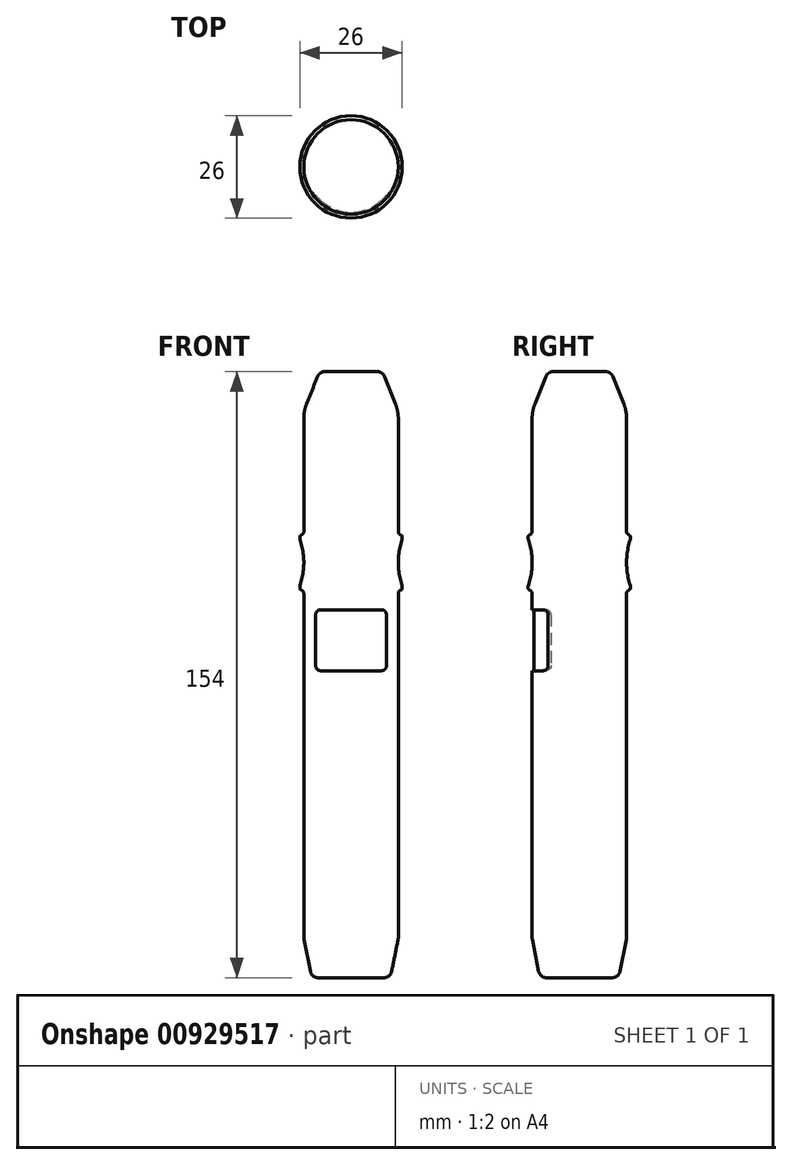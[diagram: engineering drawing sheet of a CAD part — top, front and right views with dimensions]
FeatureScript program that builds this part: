
annotation { "Feature Type Name" : "Feature", "Feature Type Description" : "" }
export const myFeature = defineFeature(function(context is Context, id is Id, definition is map)
    precondition{}
    {
        {
            var Q0;
            Q0=qCreatedBy(makeId("Top.planeOp"),FACE);
            var sketch = newSketch(context, id + "F0", { "sketchPlane" : qUnion([Q0])});
            skCircle(sketch, "E0", {"center": v(0, 0) * mm, "radius": 12 * mm});
            skSolve(sketch);
        }
        {
            var Q0;
            Q0 = qSketchRegion(id + "F0", true);
            extrude(context, id + "F1", {"entities" : qUnion([Q0]), "depth" : 154 * mm, "offsetDistance" : 25 * mm});
        }
        {
            var Q0;
            Q0=makeQuery(id+"F1.opExtrude","CAP_EDGE",EDGE,{"disambiguationData":[OSD([sQuery(id+"F0.wireOp",EDGE,"E0")])],"isStart":true});
            chamfer(context, id + "F2", {"entities" : qUnion([Q0]), "chamferType" : ChamferType.TWO_OFFSETS, "width1" : 10 * mm, "oppositeDirection" : false, "width2" : 2 * mm, "tangentPropagation" : true});
        }
        {
            var Q0;
            Q0=makeQuery(id+"F1.opExtrude","CAP_EDGE",EDGE,{"disambiguationData":[OSD([sQuery(id+"F0.wireOp",EDGE,"E0")])],"isStart":false});
            chamfer(context, id + "F3", {"entities" : qUnion([Q0]), "chamferType" : ChamferType.TWO_OFFSETS, "width1" : 4 * mm, "oppositeDirection" : false, "width2" : 10 * mm, "tangentPropagation" : true});
        }
        {
            var Q0;
            Q0=qCreatedBy(makeId("Front.planeOp"),FACE);
            var sketch = newSketch(context, id + "F4", { "sketchPlane" : qUnion([Q0])});
            skLineSegment(sketch, "E1", {"start": v(0, 112.5) * mm, "end": v(-12.5, 112.5) * mm});
            skLineSegment(sketch, "E2", {"start": v(-13, 112) * mm, "end": v(-13, 111.5) * mm});
            skLineSegment(sketch, "E3", {"start": v(-13, 99.5) * mm, "end": v(-13, 99) * mm});
            skLineSegment(sketch, "E4", {"start": v(-12.5, 98.5) * mm, "end": v(0, 98.5) * mm});
            skLineSegment(sketch, "E5", {"start": v(0, 98.5) * mm, "end": v(0, 112.5) * mm});
            skLineSegment(sketch, "E6", {"start": v(-12, 10) * mm, "end": v(-12, 110) * mm, "construction": true});
            skArc(sketch, "E7", {"start": v(-13, 99.5) * mm, "mid": v(-12, 105.5) * mm, "end": v(-13, 111.5) * mm});
            skPoint(sketch, "E8.visualSharp", {"position": v(-13, 112.5) * mm});
            skArc(sketch, "E8.filletArc", {"start": v(-12.5, 112.5) * mm, "mid": v(-12.85, 112.35) * mm, "end": v(-13, 112) * mm});
            skPoint(sketch, "E9.visualSharp", {"position": v(-13, 98.5) * mm});
            skArc(sketch, "E9.filletArc", {"start": v(-13, 99) * mm, "mid": v(-12.85, 98.65) * mm, "end": v(-12.5, 98.5) * mm});
            skSolve(sketch);
        }
        {
            var Q0;
            Q0 = qSketchRegion(id + "F4", true);
            var Q1;
            Q1=sQuery(id+"F4.wireOp",EDGE,"E5");
            revolve(context, id + "F5", {"operationType" : NewBodyOperationType.ADD, "surfaceOperationType" : NewSurfaceOperationType.NEW, "entities" : qUnion([Q0]), "axis" : qUnion([Q1]), "revolveType" : RevolveType.FULL});
        }
        {
            var Q0;
            Q0=makeQuery(id+"F5.opRevolve","SWEPT_EDGE",EDGE,{"disambiguationData":[OSD([sQuery(id+"F4.wireOp",EDGE,"E1"),sQuery(id+"F4.wireOp",EDGE,"E2")])]});
            var Q1;
            Q1=makeQuery(id+"F5.opRevolve","SWEPT_EDGE",EDGE,{"disambiguationData":[OSD([sQuery(id+"F4.wireOp",EDGE,"E2"),sQuery(id+"F4.wireOp",EDGE,"noVHmOIS-iAvs-KDMn-7KQd-Wlyn27HH3uOn")])]});
            var Q2;
            Q2=makeQuery(id+"F5.opRevolve","SWEPT_EDGE",EDGE,{"disambiguationData":[OSD([sQuery(id+"F4.wireOp",EDGE,"rKwzJUQm-pqnW-oJ42-K8gI-ygzuSZhMsq8l"),sQuery(id+"F4.wireOp",EDGE,"E3")])]});
            var Q3;
            Q3=makeQuery(id+"F5.opRevolve","SWEPT_EDGE",EDGE,{"disambiguationData":[OSD([sQuery(id+"F4.wireOp",EDGE,"E3"),sQuery(id+"F4.wireOp",EDGE,"E4")])]});
            var Q4;
            Q4=makeQuery(id+"F5.opRevolve","SWEPT_EDGE",EDGE,{"disambiguationData":[OSD([sQuery(id+"F4.wireOp",EDGE,"vrmqeYjg-Eb0b-bUPp-PHIE-IZj6HfNofiIo"),sQuery(id+"F4.wireOp",EDGE,"rKwzJUQm-pqnW-oJ42-K8gI-ygzuSZhMsq8l")])]});
            var Q5;
            Q5=makeQuery(id+"F5.opRevolve","SWEPT_EDGE",EDGE,{"disambiguationData":[OSD([sQuery(id+"F4.wireOp",EDGE,"noVHmOIS-iAvs-KDMn-7KQd-Wlyn27HH3uOn"),sQuery(id+"F4.wireOp",EDGE,"vrmqeYjg-Eb0b-bUPp-PHIE-IZj6HfNofiIo")])]});
            var Q6;
            Q6=makeQuery(id+"F5.boolean.opBoolean","INTERSECT",EDGE,{"derivedFrom":[makeQuery(id+"F1.opExtrude","SWEPT_FACE",FACE,{"disambiguationData":[OSD([sQuery(id+"F0.wireOp",EDGE,"E0")])]}),makeQuery(id+"F5.opRevolve","SWEPT_FACE",FACE,{"disambiguationData":[OSD([sQuery(id+"F4.wireOp",EDGE,"E1")])]})]});
            var Q7;
            Q7=makeQuery(id+"F5.boolean.opBoolean","INTERSECT",EDGE,{"derivedFrom":[makeQuery(id+"F1.opExtrude","SWEPT_FACE",FACE,{"disambiguationData":[OSD([sQuery(id+"F0.wireOp",EDGE,"E0")])]}),makeQuery(id+"F5.opRevolve","SWEPT_FACE",FACE,{"disambiguationData":[OSD([sQuery(id+"F4.wireOp",EDGE,"E4")])]})]});
            fillet(context, id + "F6", {"entities" : qUnion([Q0, Q1, Q2, Q3, Q4, Q5, Q6, Q7]), "radius" : 1 * mm, "tangentPropagation" : true, "allowEdgeOverflow" : false});
        }
        {
            var Q0;
            {var subQ0=sQuery(id+"F0.wireOp",EDGE,"E0");Q0=makeQuery(id+"F3.opChamfer","BLEND_EDGE",EDGE,{"blendedFrom":[makeQuery(id+"F1.opExtrude","CAP_EDGE",EDGE,{"disambiguationData":[OSD([subQ0])],"isStart":false}),makeQuery(id+"F1.opExtrude","SWEPT_FACE",FACE,{"disambiguationData":[OSD([subQ0])]})],"blendedInto":[makeQuery(id+"F1.opExtrude","SWEPT_FACE",FACE,{"disambiguationData":[OSD([subQ0])]})]});}
            fillet(context, id + "F7", {"entities" : qUnion([Q0]), "radius" : 10 * mm, "tangentPropagation" : true, "allowEdgeOverflow" : false});
        }
        {
            var Q0;
            {var subQ0=sQuery(id+"F0.wireOp",EDGE,"E0");Q0=makeQuery(id+"F3.opChamfer","BLEND_EDGE",EDGE,{"blendedFrom":[makeQuery(id+"F1.opExtrude","CAP_EDGE",EDGE,{"disambiguationData":[OSD([subQ0])],"isStart":false}),makeQuery(id+"F1.opExtrude","CAP_FACE",FACE,{"disambiguationData":[OSD([subQ0])],"isStart":false})],"blendedInto":[makeQuery(id+"F1.opExtrude","CAP_FACE",FACE,{"disambiguationData":[OSD([subQ0])],"isStart":false})]});}
            var Q1;
            {var subQ0=sQuery(id+"F0.wireOp",EDGE,"E0");Q1=makeQuery(id+"F2.opChamfer","BLEND_EDGE",EDGE,{"blendedFrom":[makeQuery(id+"F1.opExtrude","CAP_EDGE",EDGE,{"disambiguationData":[OSD([subQ0])],"isStart":true}),makeQuery(id+"F1.opExtrude","SWEPT_FACE",FACE,{"disambiguationData":[OSD([subQ0])]})],"blendedInto":[makeQuery(id+"F1.opExtrude","SWEPT_FACE",FACE,{"disambiguationData":[OSD([subQ0])]})]});}
            var Q2;
            {var subQ0=sQuery(id+"F0.wireOp",EDGE,"E0");Q2=makeQuery(id+"F2.opChamfer","BLEND_EDGE",EDGE,{"blendedFrom":[makeQuery(id+"F1.opExtrude","CAP_EDGE",EDGE,{"disambiguationData":[OSD([subQ0])],"isStart":true}),makeQuery(id+"F1.opExtrude","CAP_FACE",FACE,{"disambiguationData":[OSD([subQ0])],"isStart":true})],"blendedInto":[makeQuery(id+"F1.opExtrude","CAP_FACE",FACE,{"disambiguationData":[OSD([subQ0])],"isStart":true})]});}
            fillet(context, id + "F8", {"entities" : qUnion([Q0, Q1, Q2]), "radius" : 2 * mm, "tangentPropagation" : true, "allowEdgeOverflow" : false});
        }
        {
            var Q0;
            Q0=makeQuery(id+"F1.opExtrude","CAP_FACE",FACE,{"disambiguationData":[OSD([sQuery(id+"F0.wireOp",EDGE,"E0")])],"isStart":true});
            cPlane(context, id + "F9", {"entities" : qUnion([Q0]), "cplaneType" : CPlaneType.OFFSET, "offset" : 78 * mm, "oppositeDirection" : true, "width" : 150 * mm, "height" : 150 * mm});
        }
        {
            var Q0;
            Q0=qCreatedBy(id+"F9.planeOp",FACE);
            var sketch = newSketch(context, id + "F10", { "sketchPlane" : qUnion([Q0])});
            skArc(sketch, "E10.0", {"start": v(9, 7.16) * mm, "mid": v(0, 11.5) * mm, "end": v(-9, 7.16) * mm});
            skArc(sketch, "E11", {"start": v(9, 7.94) * mm, "mid": v(0, 12) * mm, "end": v(-9, 7.94) * mm});
            skLineSegment(sketch, "E12", {"start": v(-9, 7.94) * mm, "end": v(-9, 7.16) * mm});
            skLineSegment(sketch, "E13", {"start": v(9, 7.94) * mm, "end": v(9, 7.16) * mm});
            skSolve(sketch);
        }
        {
            var Q0;
            Q0 = qSketchRegion(id + "F10", true);
            extrude(context, id + "F11", {"entities" : qUnion([Q0]), "operationType" : NewBodyOperationType.REMOVE, "oppositeDirection" : true, "depth" : 15.5 * mm, "offsetDistance" : 25 * mm});
        }
        {
            var Q0;
            Q0=makeQuery(id+"F11.boolean.opBoolean","COPY",EDGE,{"derivedFrom":makeQuery(id+"F11.opExtrude","CAP_EDGE",EDGE,{"disambiguationData":[OSD([sQuery(id+"F10.wireOp",EDGE,"E12")])],"isStart":false})});
            var Q1;
            Q1=makeQuery(id+"F11.boolean.opBoolean","COPY",EDGE,{"derivedFrom":makeQuery(id+"F11.opExtrude","CAP_EDGE",EDGE,{"disambiguationData":[OSD([sQuery(id+"F10.wireOp",EDGE,"E13")])],"isStart":false})});
            var Q2;
            Q2=makeQuery(id+"F11.boolean.opBoolean","COPY",EDGE,{"derivedFrom":makeQuery(id+"F11.opExtrude","CAP_EDGE",EDGE,{"disambiguationData":[OSD([sQuery(id+"F10.wireOp",EDGE,"E13")])],"isStart":true})});
            var Q3;
            Q3=makeQuery(id+"F11.boolean.opBoolean","COPY",EDGE,{"derivedFrom":makeQuery(id+"F11.opExtrude","CAP_EDGE",EDGE,{"disambiguationData":[OSD([sQuery(id+"F10.wireOp",EDGE,"E12")])],"isStart":true})});
            fillet(context, id + "F12", {"entities" : qUnion([Q0, Q1, Q2, Q3]), "radius" : 1.3 * mm, "tangentPropagation" : true, "allowEdgeOverflow" : false});
        }
    });
